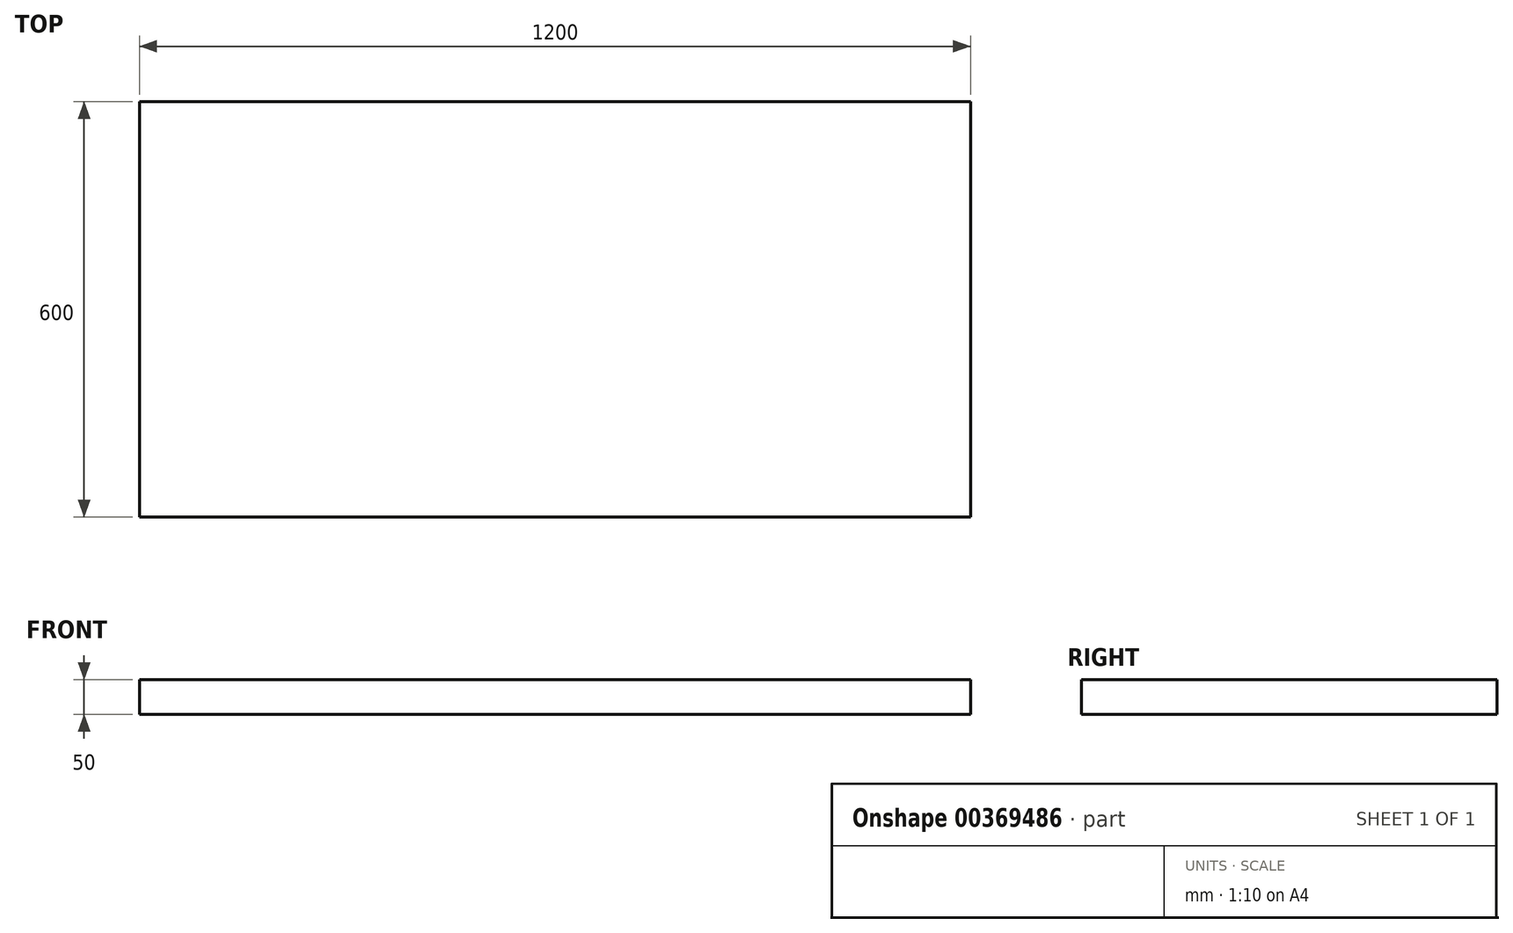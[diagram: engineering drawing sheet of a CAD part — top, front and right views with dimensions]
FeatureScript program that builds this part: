
annotation { "Feature Type Name" : "Feature", "Feature Type Description" : "" }
export const myFeature = defineFeature(function(context is Context, id is Id, definition is map)
    precondition{}
    {
        {
            var Q0;
            Q0=qCreatedBy(makeId("Top.planeOp"),FACE);
            var sketch = newSketch(context, id + "F0", { "sketchPlane" : qUnion([Q0])});
            skLineSegment(sketch, "E0.bottom", {"start": v(-591, 240.23) * mm, "end": v(609, 240.23) * mm});
            skLineSegment(sketch, "E0.top", {"start": v(-591, -359.77) * mm, "end": v(609, -359.77) * mm});
            skLineSegment(sketch, "E0.left", {"start": v(-591, 240.23) * mm, "end": v(-591, -359.77) * mm});
            skLineSegment(sketch, "E0.right", {"start": v(609, 240.23) * mm, "end": v(609, -359.77) * mm});
            skSolve(sketch);
        }
        {
            var Q0;
            Q0=makeQuery(id+"F0.imprint","IMPRINT",FACE,{"disambiguationData":[TD([[makeQuery(id+"F0.imprint","IMPRINT",EDGE,{"derivedFrom":sQuery(id+"F0.wireOp",EDGE,"E0.bottom")}),-1.0]])]});
            extrude(context, id + "F1", {"entities" : qUnion([Q0]), "depth" : 50 * mm});
        }
    });
